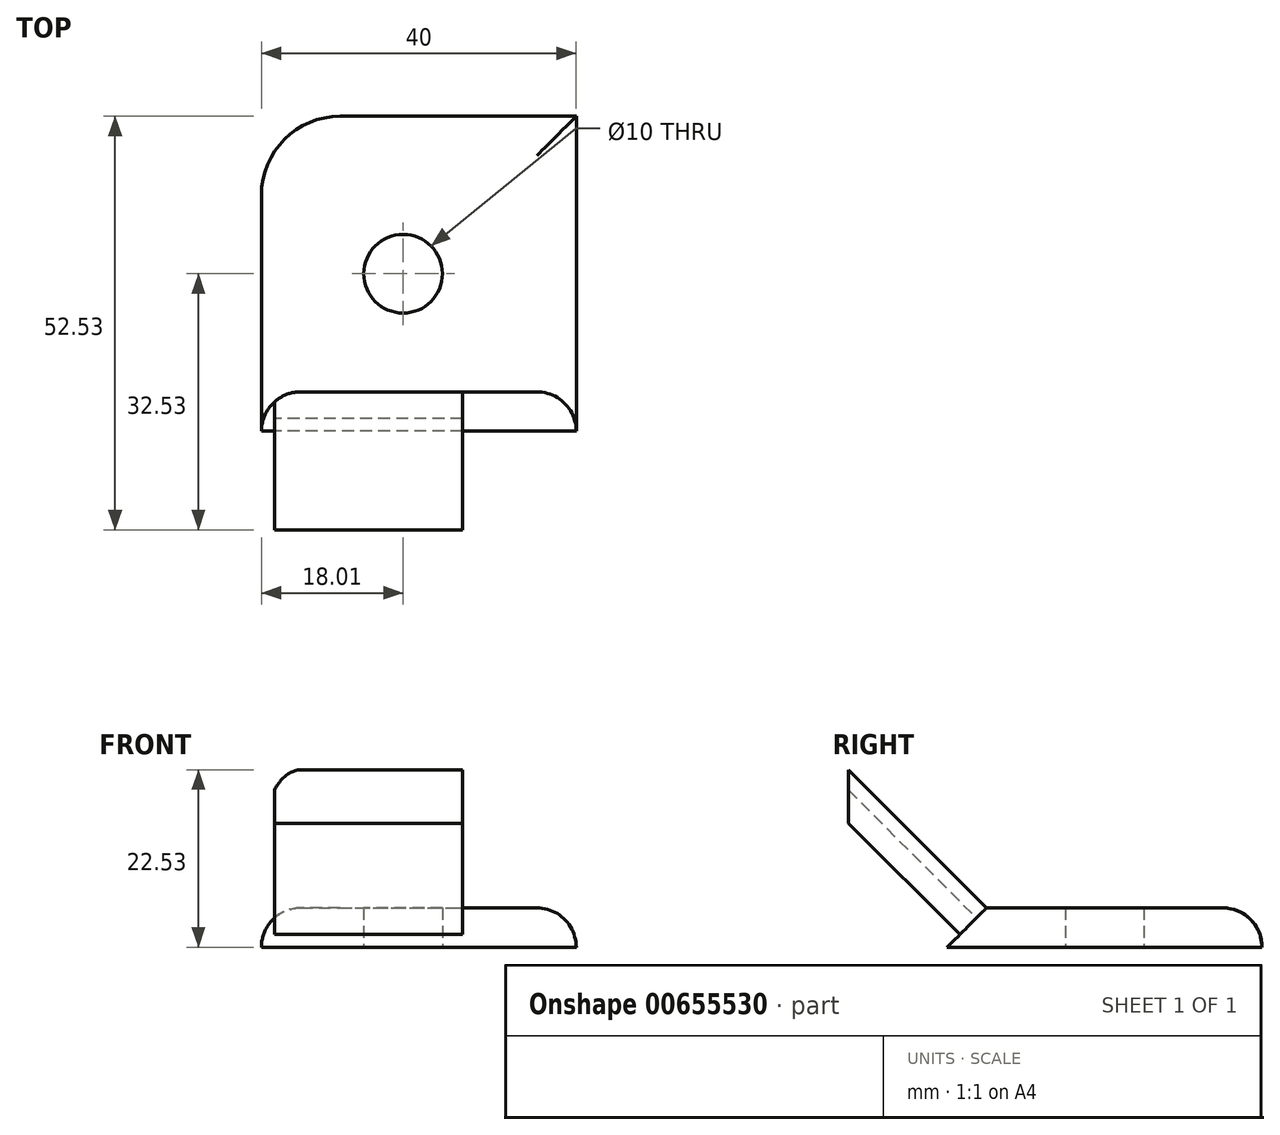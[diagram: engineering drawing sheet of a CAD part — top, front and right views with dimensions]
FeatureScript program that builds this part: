
annotation { "Feature Type Name" : "Feature", "Feature Type Description" : "" }
export const myFeature = defineFeature(function(context is Context, id is Id, definition is map)
    precondition{}
    {
        {
            var Q0;
            Q0=qCreatedBy(makeId("Top.planeOp"),FACE);
            var sketch = newSketch(context, id + "F0", { "sketchPlane" : qUnion([Q0])});
            skLineSegment(sketch, "E0.bottom", {"start": v(22, -20) * mm, "end": v(-18, -20) * mm});
            skLineSegment(sketch, "E0.top", {"start": v(22, 20) * mm, "end": v(-8, 20) * mm});
            skLineSegment(sketch, "E0.left", {"start": v(22, -20) * mm, "end": v(22, 20) * mm});
            skLineSegment(sketch, "E0.right", {"start": v(-18, -20) * mm, "end": v(-18, 10) * mm});
            skPoint(sketch, "E0.middle", {"position": v(2, 0) * mm});
            skCircle(sketch, "E1", {"center": v(0, 0) * mm, "radius": 5 * mm});
            skPoint(sketch, "E2.visualSharp", {"position": v(-18, 20) * mm});
            skArc(sketch, "E2.filletArc", {"start": v(-8, 20) * mm, "mid": v(-15.08, 17.07) * mm, "end": v(-18, 10) * mm});
            skSolve(sketch);
        }
        {
            var Q0;
            Q0=makeQuery(id+"F0.imprint","IMPRINT",FACE,{"disambiguationData":[TD([[makeQuery(id+"F0.imprint","IMPRINT",EDGE,{"derivedFrom":sQuery(id+"F0.wireOp",EDGE,"E0.bottom")}),-1.0]])]});
            extrude(context, id + "F1", {"entities" : qUnion([Q0]), "depth" : 5 * mm, "offsetDistance" : 25 * mm});
        }
        {
            var Q0;
            Q0=makeQuery(id+"F1.opExtrude","CAP_EDGE",EDGE,{"disambiguationData":[OSD([sQuery(id+"F0.wireOp",EDGE,"E0.bottom")])],"isStart":false});
            chamfer(context, id + "F2", {"entities" : qUnion([Q0]), "width" : 5 * mm, "tangentPropagation" : true});
        }
        {
            var Q0;
            Q0=makeQuery(id+"F1.opExtrude","CAP_EDGE",EDGE,{"disambiguationData":[OSD([sQuery(id+"F0.wireOp",EDGE,"E0.top")])],"isStart":false});
            chamfer(context, id + "F3", {"entities" : qUnion([Q0]), "chamferType" : ChamferType.TWO_OFFSETS, "width1" : 2 * mm, "oppositeDirection" : false, "width2" : 3 * mm});
        }
        {
            var Q0;
            Q0=makeQuery(id+"F1.opExtrude","CAP_EDGE",EDGE,{"disambiguationData":[OSD([sQuery(id+"F0.wireOp",EDGE,"E0.left")])],"isStart":false});
            var Q1;
            Q1=makeQuery(id+"F1.opExtrude","CAP_EDGE",EDGE,{"disambiguationData":[OSD([sQuery(id+"F0.wireOp",EDGE,"E0.right")])],"isStart":false});
            fillet(context, id + "F4", {"entities" : qUnion([Q0, Q1]), "radius" : 5 * mm, "tangentPropagation" : true, "allowEdgeOverflow" : false});
        }
        {
            var Q0;
            Q0=makeQuery(id+"F2.opChamfer","BLEND_FACE",FACE,{"disambiguationData":[OSD([sQuery(id+"F0.wireOp",EDGE,"E0.bottom")])]});
            var sketch = newSketch(context, id + "F5", { "sketchPlane" : qUnion([Q0])});
            skLineSegment(sketch, "E3.bottom", {"start": v(7.54, -11.87) * mm, "end": v(-16.35, -11.87) * mm});
            skLineSegment(sketch, "E3.top", {"start": v(7.54, -6.8) * mm, "end": v(-16.35, -6.8) * mm});
            skLineSegment(sketch, "E3.left", {"start": v(7.54, -11.87) * mm, "end": v(7.54, -6.8) * mm});
            skLineSegment(sketch, "E3.right", {"start": v(-16.35, -11.87) * mm, "end": v(-16.35, -6.8) * mm});
            skPoint(sketch, "E3.middle", {"position": v(-4.4, -9.33) * mm});
            skSolve(sketch);
        }
        {
            var Q0;
            {var subQ8=sQuery(id+"F5.wireOp",EDGE,"E3.bottom");Q0=makeQuery(id+"F5.imprint","IMPRINT",FACE,{"disambiguationData":[TD([[makeQuery(id+"F5.imprint","IMPRINT",EDGE,{"derivedFrom":subQ8}),-1.0]])]});}
            extrude(context, id + "F6", {"entities" : qUnion([Q0]), "operationType" : NewBodyOperationType.ADD, "depth" : 25 * mm, "offsetDistance" : 25 * mm});
        }
        {
            var Q0;
            Q0=makeQuery(id+"F6.opExtrude","CAP_EDGE",EDGE,{"disambiguationData":[OSD([sQuery(id+"F5.wireOp",EDGE,"E3.bottom")])],"isStart":false});
            chamfer(context, id + "F7", {"entities" : qUnion([Q0]), "width" : 5 * mm, "tangentPropagation" : true});
        }
    });
